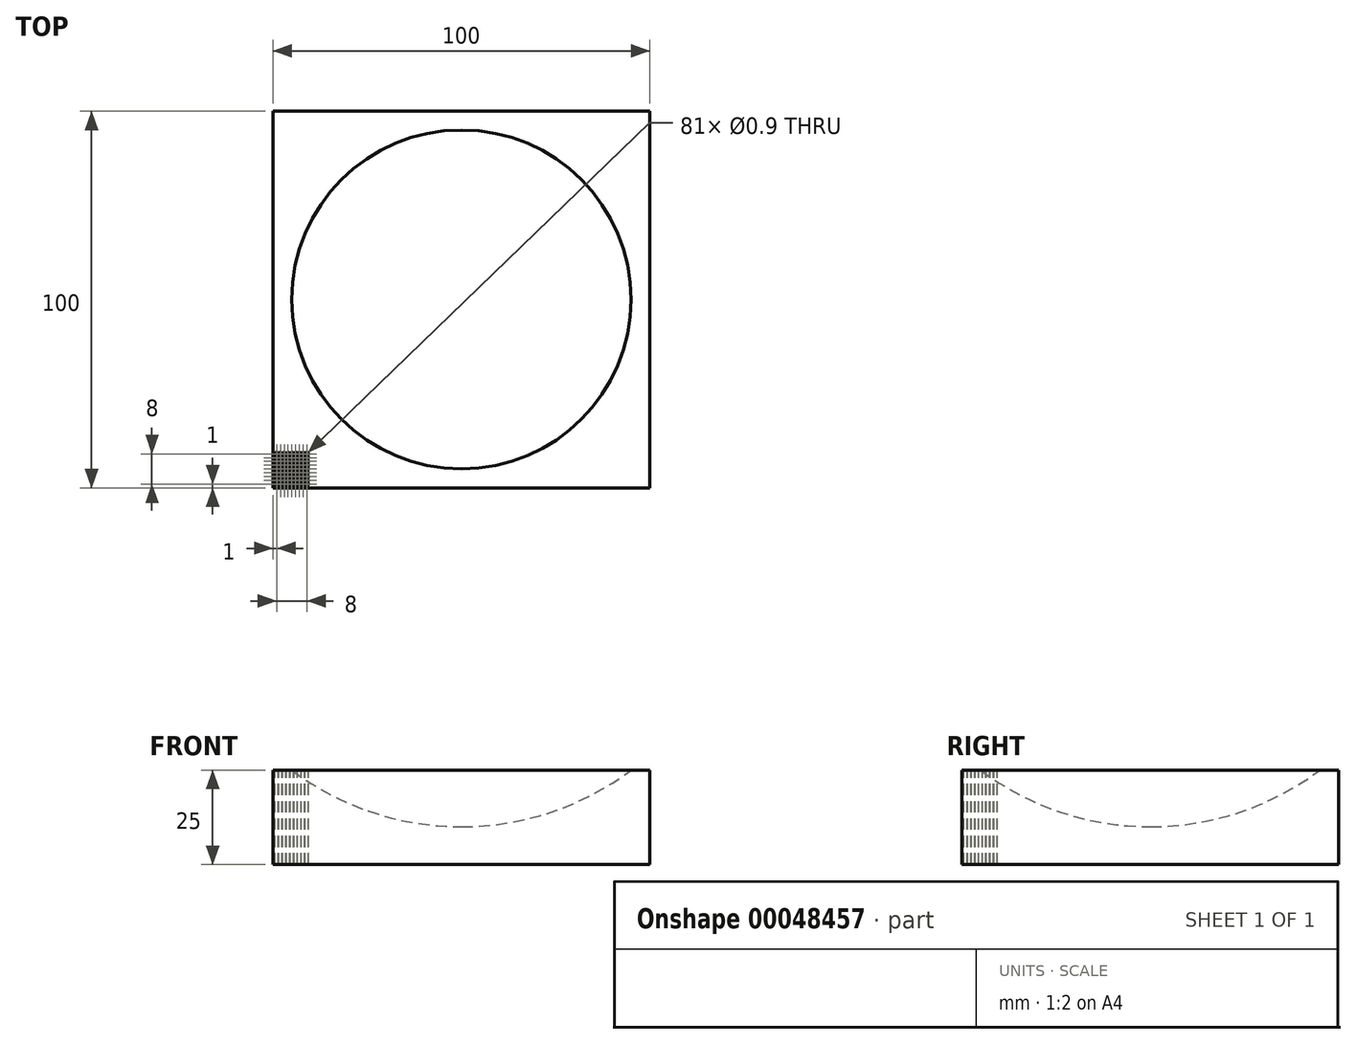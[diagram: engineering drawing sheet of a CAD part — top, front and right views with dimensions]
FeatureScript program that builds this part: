
annotation { "Feature Type Name" : "Feature", "Feature Type Description" : "" }
export const myFeature = defineFeature(function(context is Context, id is Id, definition is map)
    precondition{}
    {
        {
            var Q0;
            Q0=qCreatedBy(makeId("Top.planeOp"),FACE);
            var sketch = newSketch(context, id + "F0", { "sketchPlane" : qUnion([Q0])});
            skLineSegment(sketch, "E0.rect.bottom", {"start": v(50, -50) * mm, "end": v(-50, -50) * mm});
            skLineSegment(sketch, "E0.rect.top", {"start": v(50, 50) * mm, "end": v(-50, 50) * mm});
            skLineSegment(sketch, "E0.rect.left", {"start": v(50, -50) * mm, "end": v(50, 50) * mm});
            skLineSegment(sketch, "E0.rect.right", {"start": v(-50, -50) * mm, "end": v(-50, 50) * mm});
            skPoint(sketch, "E0.rect.middle", {"position": v(0, 0) * mm});
            skSolve(sketch);
        }
        {
            var Q0;
            Q0=makeQuery(id+"F0.imprint","IMPRINT",FACE,{"disambiguationData":[TD([[makeQuery(id+"F0.imprint","IMPRINT",EDGE,{"derivedFrom":sQuery(id+"F0.wireOp",EDGE,"E0.rect.bottom")}),-1.0]])]});
            extrude(context, id + "F1", {"entities" : qUnion([Q0]), "depth" : 25 * mm});
        }
        {
            var Q0;
            Q0=makeQuery(id+"F1.opExtrude","CAP_FACE",FACE,{"disambiguationData":[OSD([sQuery(id+"F0.wireOp",EDGE,"E0.rect.bottom"),sQuery(id+"F0.wireOp",EDGE,"E0.rect.top"),sQuery(id+"F0.wireOp",EDGE,"E0.rect.left"),sQuery(id+"F0.wireOp",EDGE,"E0.rect.right")])],"isStart":false});
            var sketch = newSketch(context, id + "F2", { "sketchPlane" : qUnion([Q0])});
            skCircle(sketch, "E1", {"center": v(-49, -49) * mm, "radius": 0.45 * mm});
            skCircle(sketch, "E2.0.1.0", {"center": v(-49, -48) * mm, "radius": 0.45 * mm});
            skCircle(sketch, "E2.0.2.0", {"center": v(-49, -47) * mm, "radius": 0.45 * mm});
            skCircle(sketch, "E2.0.3.0", {"center": v(-49, -46) * mm, "radius": 0.45 * mm});
            skCircle(sketch, "E2.0.4.0", {"center": v(-49, -45) * mm, "radius": 0.45 * mm});
            skCircle(sketch, "E2.0.5.0", {"center": v(-49, -44) * mm, "radius": 0.45 * mm});
            skCircle(sketch, "E2.0.6.0", {"center": v(-49, -43) * mm, "radius": 0.45 * mm});
            skCircle(sketch, "E2.0.7.0", {"center": v(-49, -42) * mm, "radius": 0.45 * mm});
            skCircle(sketch, "E2.0.8.0", {"center": v(-49, -41) * mm, "radius": 0.45 * mm});
            skCircle(sketch, "E2.1.0.0", {"center": v(-48, -49) * mm, "radius": 0.45 * mm});
            skCircle(sketch, "E2.1.1.0", {"center": v(-48, -48) * mm, "radius": 0.45 * mm});
            skCircle(sketch, "E2.1.2.0", {"center": v(-48, -47) * mm, "radius": 0.45 * mm});
            skCircle(sketch, "E2.1.3.0", {"center": v(-48, -46) * mm, "radius": 0.45 * mm});
            skCircle(sketch, "E2.1.4.0", {"center": v(-48, -45) * mm, "radius": 0.45 * mm});
            skCircle(sketch, "E2.1.5.0", {"center": v(-48, -44) * mm, "radius": 0.45 * mm});
            skCircle(sketch, "E2.1.6.0", {"center": v(-48, -43) * mm, "radius": 0.45 * mm});
            skCircle(sketch, "E2.1.7.0", {"center": v(-48, -42) * mm, "radius": 0.45 * mm});
            skCircle(sketch, "E2.1.8.0", {"center": v(-48, -41) * mm, "radius": 0.45 * mm});
            skCircle(sketch, "E2.2.0.0", {"center": v(-47, -49) * mm, "radius": 0.45 * mm});
            skCircle(sketch, "E2.2.1.0", {"center": v(-47, -48) * mm, "radius": 0.45 * mm});
            skCircle(sketch, "E2.2.2.0", {"center": v(-47, -47) * mm, "radius": 0.45 * mm});
            skCircle(sketch, "E2.2.3.0", {"center": v(-47, -46) * mm, "radius": 0.45 * mm});
            skCircle(sketch, "E2.2.4.0", {"center": v(-47, -45) * mm, "radius": 0.45 * mm});
            skCircle(sketch, "E2.2.5.0", {"center": v(-47, -44) * mm, "radius": 0.45 * mm});
            skCircle(sketch, "E2.2.6.0", {"center": v(-47, -43) * mm, "radius": 0.45 * mm});
            skCircle(sketch, "E2.2.7.0", {"center": v(-47, -42) * mm, "radius": 0.45 * mm});
            skCircle(sketch, "E2.2.8.0", {"center": v(-47, -41) * mm, "radius": 0.45 * mm});
            skCircle(sketch, "E2.3.0.0", {"center": v(-46, -49) * mm, "radius": 0.45 * mm});
            skCircle(sketch, "E2.3.1.0", {"center": v(-46, -48) * mm, "radius": 0.45 * mm});
            skCircle(sketch, "E2.3.2.0", {"center": v(-46, -47) * mm, "radius": 0.45 * mm});
            skCircle(sketch, "E2.3.3.0", {"center": v(-46, -46) * mm, "radius": 0.45 * mm});
            skCircle(sketch, "E2.3.4.0", {"center": v(-46, -45) * mm, "radius": 0.45 * mm});
            skCircle(sketch, "E2.3.5.0", {"center": v(-46, -44) * mm, "radius": 0.45 * mm});
            skCircle(sketch, "E2.3.6.0", {"center": v(-46, -43) * mm, "radius": 0.45 * mm});
            skCircle(sketch, "E2.3.7.0", {"center": v(-46, -42) * mm, "radius": 0.45 * mm});
            skCircle(sketch, "E2.3.8.0", {"center": v(-46, -41) * mm, "radius": 0.45 * mm});
            skCircle(sketch, "E2.4.0.0", {"center": v(-45, -49) * mm, "radius": 0.45 * mm});
            skCircle(sketch, "E2.4.1.0", {"center": v(-45, -48) * mm, "radius": 0.45 * mm});
            skCircle(sketch, "E2.4.2.0", {"center": v(-45, -47) * mm, "radius": 0.45 * mm});
            skCircle(sketch, "E2.4.3.0", {"center": v(-45, -46) * mm, "radius": 0.45 * mm});
            skCircle(sketch, "E2.4.4.0", {"center": v(-45, -45) * mm, "radius": 0.45 * mm});
            skCircle(sketch, "E2.4.5.0", {"center": v(-45, -44) * mm, "radius": 0.45 * mm});
            skCircle(sketch, "E2.4.6.0", {"center": v(-45, -43) * mm, "radius": 0.45 * mm});
            skCircle(sketch, "E2.4.7.0", {"center": v(-45, -42) * mm, "radius": 0.45 * mm});
            skCircle(sketch, "E2.4.8.0", {"center": v(-45, -41) * mm, "radius": 0.45 * mm});
            skCircle(sketch, "E2.5.0.0", {"center": v(-44, -49) * mm, "radius": 0.45 * mm});
            skCircle(sketch, "E2.5.1.0", {"center": v(-44, -48) * mm, "radius": 0.45 * mm});
            skCircle(sketch, "E2.5.2.0", {"center": v(-44, -47) * mm, "radius": 0.45 * mm});
            skCircle(sketch, "E2.5.3.0", {"center": v(-44, -46) * mm, "radius": 0.45 * mm});
            skCircle(sketch, "E2.5.4.0", {"center": v(-44, -45) * mm, "radius": 0.45 * mm});
            skCircle(sketch, "E2.5.5.0", {"center": v(-44, -44) * mm, "radius": 0.45 * mm});
            skCircle(sketch, "E2.5.6.0", {"center": v(-44, -43) * mm, "radius": 0.45 * mm});
            skCircle(sketch, "E2.5.7.0", {"center": v(-44, -42) * mm, "radius": 0.45 * mm});
            skCircle(sketch, "E2.5.8.0", {"center": v(-44, -41) * mm, "radius": 0.45 * mm});
            skCircle(sketch, "E2.6.0.0", {"center": v(-43, -49) * mm, "radius": 0.45 * mm});
            skCircle(sketch, "E2.6.1.0", {"center": v(-43, -48) * mm, "radius": 0.45 * mm});
            skCircle(sketch, "E2.6.2.0", {"center": v(-43, -47) * mm, "radius": 0.45 * mm});
            skCircle(sketch, "E2.6.3.0", {"center": v(-43, -46) * mm, "radius": 0.45 * mm});
            skCircle(sketch, "E2.6.4.0", {"center": v(-43, -45) * mm, "radius": 0.45 * mm});
            skCircle(sketch, "E2.6.5.0", {"center": v(-43, -44) * mm, "radius": 0.45 * mm});
            skCircle(sketch, "E2.6.6.0", {"center": v(-43, -43) * mm, "radius": 0.45 * mm});
            skCircle(sketch, "E2.6.7.0", {"center": v(-43, -42) * mm, "radius": 0.45 * mm});
            skCircle(sketch, "E2.6.8.0", {"center": v(-43, -41) * mm, "radius": 0.45 * mm});
            skCircle(sketch, "E2.7.0.0", {"center": v(-42, -49) * mm, "radius": 0.45 * mm});
            skCircle(sketch, "E2.7.1.0", {"center": v(-42, -48) * mm, "radius": 0.45 * mm});
            skCircle(sketch, "E2.7.2.0", {"center": v(-42, -47) * mm, "radius": 0.45 * mm});
            skCircle(sketch, "E2.7.3.0", {"center": v(-42, -46) * mm, "radius": 0.45 * mm});
            skCircle(sketch, "E2.7.4.0", {"center": v(-42, -45) * mm, "radius": 0.45 * mm});
            skCircle(sketch, "E2.7.5.0", {"center": v(-42, -44) * mm, "radius": 0.45 * mm});
            skCircle(sketch, "E2.7.6.0", {"center": v(-42, -43) * mm, "radius": 0.45 * mm});
            skCircle(sketch, "E2.7.7.0", {"center": v(-42, -42) * mm, "radius": 0.45 * mm});
            skCircle(sketch, "E2.7.8.0", {"center": v(-42, -41) * mm, "radius": 0.45 * mm});
            skCircle(sketch, "E2.8.0.0", {"center": v(-41, -49) * mm, "radius": 0.45 * mm});
            skCircle(sketch, "E2.8.1.0", {"center": v(-41, -48) * mm, "radius": 0.45 * mm});
            skCircle(sketch, "E2.8.2.0", {"center": v(-41, -47) * mm, "radius": 0.45 * mm});
            skCircle(sketch, "E2.8.3.0", {"center": v(-41, -46) * mm, "radius": 0.45 * mm});
            skCircle(sketch, "E2.8.4.0", {"center": v(-41, -45) * mm, "radius": 0.45 * mm});
            skCircle(sketch, "E2.8.5.0", {"center": v(-41, -44) * mm, "radius": 0.45 * mm});
            skCircle(sketch, "E2.8.6.0", {"center": v(-41, -43) * mm, "radius": 0.45 * mm});
            skCircle(sketch, "E2.8.7.0", {"center": v(-41, -42) * mm, "radius": 0.45 * mm});
            skCircle(sketch, "E2.8.8.0", {"center": v(-41, -41) * mm, "radius": 0.45 * mm});
            skLineSegment(sketch, "E2.direction1", {"start": v(-49, -49) * mm, "end": v(-48, -49) * mm, "construction": true});
            skLineSegment(sketch, "E2.direction2", {"start": v(-49, -49) * mm, "end": v(-49, -48) * mm, "construction": true});
            skSolve(sketch);
        }
        {
            var Q0;
            Q0 = qSketchRegion(id + "F2", true);
            extrude(context, id + "F3", {"entities" : qUnion([Q0]), "operationType" : NewBodyOperationType.REMOVE, "endBound" : BoundingType.THROUGH_ALL, "oppositeDirection" : true, "depth" : 25 * mm});
        }
        {
            var Q0;
            Q0=makeQuery(id+"F1.opExtrude","SWEPT_FACE",FACE,{"disambiguationData":[OSD([sQuery(id+"F0.wireOp",EDGE,"E0.rect.bottom")])]});
            cPlane(context, id + "F4", {"entities" : qUnion([Q0]), "cplaneType" : CPlaneType.OFFSET, "offset" : 50 * mm, "oppositeDirection" : true, "width" : 150 * mm, "height" : 150 * mm});
        }
        {
            var Q0;
            Q0=qCreatedBy(id+"F4.planeOp",FACE);
            var sketch = newSketch(context, id + "F5", { "sketchPlane" : qUnion([Q0])});
            skLineSegment(sketch, "E3.0", {"start": v(0, 25) * mm, "end": v(-45, 25) * mm});
            skLineSegment(sketch, "E4", {"start": v(0, 25) * mm, "end": v(0, 85) * mm, "construction": true});
            skPoint(sketch, "E4.endSnap0", {"position": v(0, 25) * mm});
            skArc(sketch, "E5", {"start": v(0, 10) * mm, "mid": v(-23.72, 13.85) * mm, "end": v(-45, 25) * mm});
            skLineSegment(sketch, "E6", {"start": v(0, 25) * mm, "end": v(0, 10) * mm});
            skSolve(sketch);
        }
        {
            var Q0;
            Q0 = qSketchRegion(id + "F5", true);
            var Q1;
            Q1=sQuery(id+"F5.wireOp",EDGE,"E4");
            revolve(context, id + "F6", {"operationType" : NewBodyOperationType.REMOVE, "entities" : qUnion([Q0]), "axis" : qUnion([Q1]), "revolveType" : RevolveType.FULL});
        }
    });
